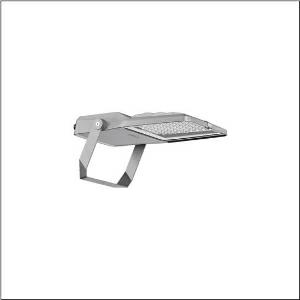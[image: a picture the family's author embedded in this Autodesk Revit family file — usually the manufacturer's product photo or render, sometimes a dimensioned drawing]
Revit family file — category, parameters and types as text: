
# Revit family: floodlight_fl_21_mini___pl61_5xa7772c1c1a_2fdc
name_source: partatom
category: Lighting Fixtures
units: mm (PartAtom-declared; Revit-internal decimal feet)

## family parameters
Cut with Voids When Loaded = No
Host = Face
Light Source = No
Part Type = Normal
Room Calculation Point = No
Round Connector Dimension = Use Diameter
Shared = No

## types (1)
- --- (1 x LED, 9930 lm, 87.2 W, 2200K)
    Apparent Load = 87 VA
    CIE Flux Codes = 33 65 98 100 100
    Color Rendering = 70
    Color Temperature = 2200K
    Default Elevation = 1800 mm
    Description = Floodlight FL 21 mini, floodlight, primary light control with lens, of PMMA, primary optical cover: protective disc, of toughened safety glass, transparent, light distribution: PL61, light emission: direct distribution, installation type: surface-mounted, LED, High Power LED, rated luminous flux: 9.930lm, luminous efficacy: 114lm/W, light colour: 722, colour temperature: 2200K, control gear: ECG iQ, control: Street-Remote, Auto-Match, Temp-Guard, Night-Set, Smart-Wire, Desk-Remote (wireless, voltage-free reading and setting of iQ features in the workshop via application-optimized NFC function/RFID function), optimised constant luminous flux control (CLO 2.0), with terminal, 6-pole, mains connection: 220..240V, AC, 50/60Hz, start of lifetime: 87W, end of lifetime: 92W, reduction: 40W, luminaire housing, of diecast aluminium, powder-coated, Siteco® metallic grey (DB 702S), corrosivity category C5 according to DIN EN ISO 12944, mounting bracket, of steel, galvanised, powder-coated, Siteco® metallic grey (DB 702S), protection rating (complete): IP66, insulation class (complete): insulation class II (safety insulation), certification: CE, ENEC, VDE, protection symbol: D, impact resistance: IK08, permissible operating ambient temperature: -40..+40°C, permissible operating ambient temperature for outdoor applications: -40..+50°C, standard: DIN EN 12944, packaging unit: 1 piece

Light Distribution: PL61
    Height = 70 mm
    Lamp = 1 x LED
    Lamp Light Flux = 9930 lm
    Lamp Power = 87.2 W
    Lamp count = 1
    Length = 485 mm
    Luminous efficacy = 114 lm/W
    Manufacturer = Siteco
    ModVariant = No
    Model = 5XA7772C1C1A
    Number of Poles = 1
    OnlyDefault = Yes
    Power Factor = 1
    Product Name = Floodlight FL 21 mini | PL61
    Product group = floodlight | pylon top
    ProductGroupID = 6101
    Protection Class = Protection class II
    Protection Degree = IP 66
    RLX_Detail_Level = 1
    RlxData = <blob elided: 95881 chars, md5=e987c1e5>
    Socket = socket
    Standby Power = 0 W
    System Light Flux = 9930 lm
    System Power = 87 W
    Type Comments = factory setting: luminous flux: 100 % | dim-lin: 254 | 456 mA
    Type Image = l_1006845.jpg
    URL = http://relux.com
    VarID = @adj_085477
    Voltage = 0 V
    Weight = 0.00 kg
    Width = 337 mm

## geometry (parser evidence)
native form markers: Blend x4, Sweep x13
no freeform markers — native parametric forms only
